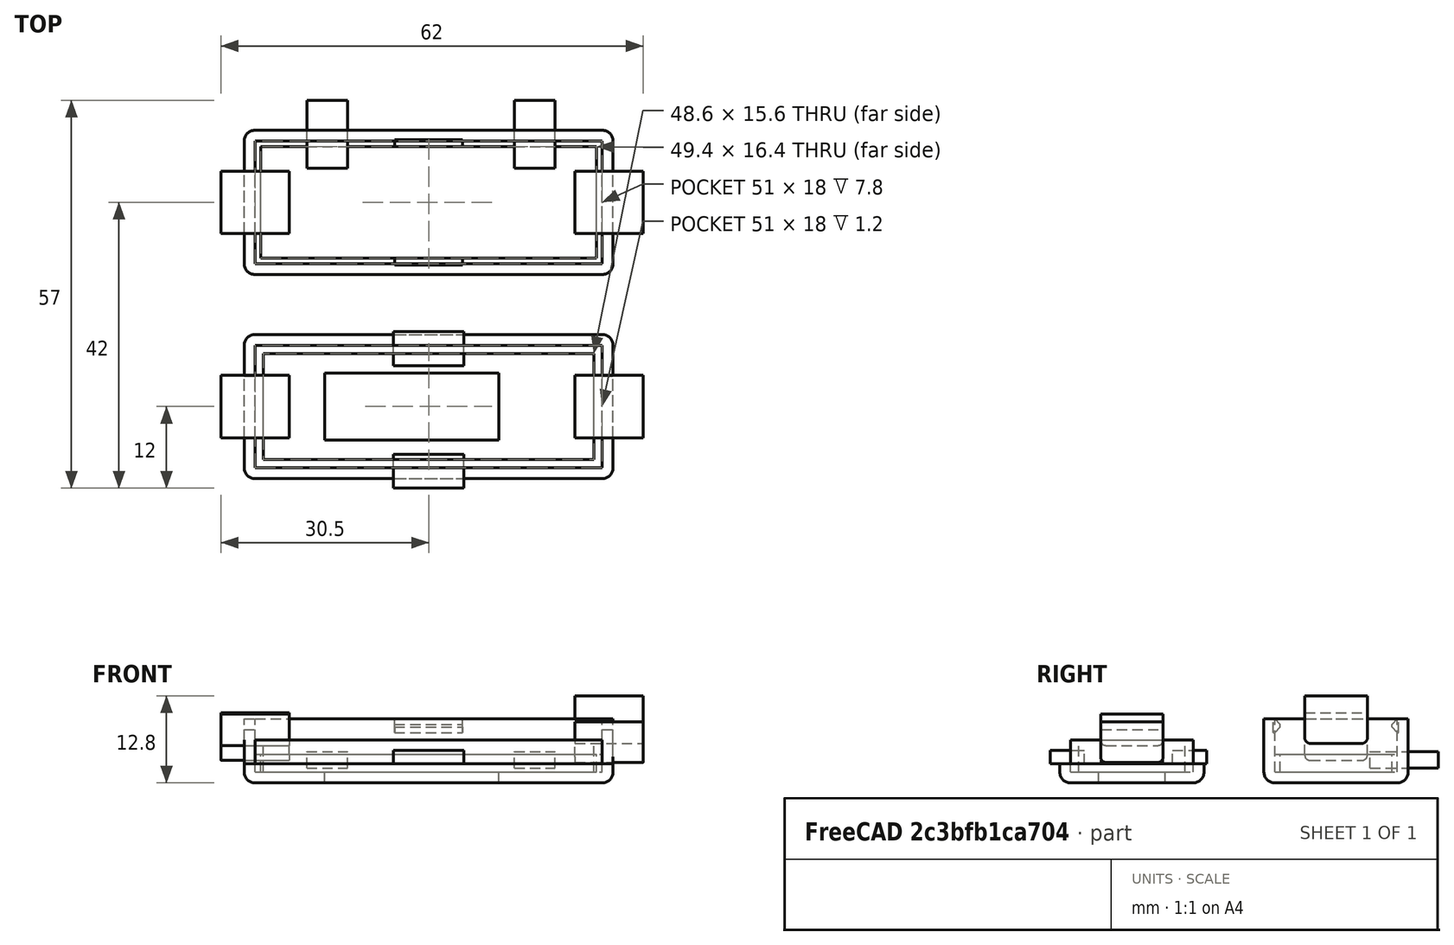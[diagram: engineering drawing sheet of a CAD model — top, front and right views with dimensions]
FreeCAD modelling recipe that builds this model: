
FCSTD DOCUMENT  (FreeCAD 0.16R)
Label: USB-C_Tester_b_raw_v0.4
License: All rights reserved
LicenseURL: http://en.wikipedia.org/wiki/All_rights_reserved
objects: Part::Box×21, Part::Fillet×6, Part::Cut×4, Part::Chamfer×2
note: 33 computed .brp shape members not serialized (recipe doc carries the construction recipe); baked Part::Feature solids carry a one-line shape summary decoded from their .brp

FEATURE [Part::Box] Box  label="unten_außen"
  Height = 9.4
  Length = 54.2
  Placement = pos=(-1.6,-1.6,0) rot=(0,0,1;0rad)
  Width = 21.2
FEATURE [Part::Box] Box001  label="unten_innen"
  Height = 9.4
  Length = 51
  Placement = pos=(0,0,1.6) rot=(0,0,1;0rad)
  Width = 18
FEATURE [Part::Cut] Cut  label="Schale_roh"
  Base = -> Box
  Tool = -> Box001
FEATURE [Part::Fillet] Fillet  label="Schale_unten"
  Base = -> Cut
  Edges = 8 edges r=1.6: [Edge1,Edge3,Edge4,Edge5,Edge6,Edge14,Edge15,Edge16]
FEATURE [Part::Box] Box002  label="Auflage_außen"
  Height = 2.6
  Length = 51
  Placement = pos=(0,0,1.6) rot=(0,0,1;0rad)
  Width = 18
FEATURE [Part::Box] Box003  label="Auflage_innen"
  Height = 2.6
  Length = 49.4
  Placement = pos=(0.8,0.8,1.6) rot=(0,0,1;0rad)
  Width = 16.4
FEATURE [Part::Cut] Cut001  label="Auflage"
  Base = -> Box002
  Tool = -> Box003
FEATURE [Part::Box] Box004  label="Haken1_roh"
  Height = 2
  Length = 10
  Placement = pos=(20.5,-0.2,7.4) rot=(0,0,1;0rad)
  Width = 1
FEATURE [Part::Chamfer] Chamfer  label="Haken1"
  Base = -> Box004
  Edges = 2 edges r=0.8: [Edge11,Edge12]
FEATURE [Part::Box] Box005  label="Haken2_roh"
  Height = 2
  Length = 10
  Placement = pos=(20.5,17.2,7.4) rot=(0,0,1;0rad)
  Width = 1
FEATURE [Part::Chamfer] Chamfer001  label="Haken2"
  Base = -> Box005
  Edges = 2 edges r=0.8: [Edge9,Edge10]
FEATURE [Part::Box] Box006  label="USB_Buchse1_roh"
  Height = 7
  Length = 10
  Placement = pos=(-5,4.4,3.3) rot=(0,0,1;0rad)
  Width = 9.2
FEATURE [Part::Box] Box008  label="Button1"
  Height = 2.4
  Length = 6
  Placement = pos=(7.6,14,2.2) rot=(0,0,1;0rad)
  Width = 10
FEATURE [Part::Box] Box009  label="Button2"
  Height = 2.4
  Length = 6
  Placement = pos=(38.1,14,2.2) rot=(0,0,1;0rad)
  Width = 10
FEATURE [Part::Box] Box010  label="oben_außen"
  Height = 2.8
  Length = 54.2
  Placement = pos=(-1.6,-31.6,0) rot=(0,0,1;0rad)
  Width = 21.2
FEATURE [Part::Box] Box011  label="oben_innen"
  Height = 9.4
  Length = 51
  Placement = pos=(0,-30,1.6) rot=(0,0,1;0rad)
  Width = 18
FEATURE [Part::Cut] Cut002  label="Schale_oben_roh"
  Base = -> Box010
  Tool = -> Box011
FEATURE [Part::Fillet] Fillet001  label="Schale_oben"
  Base = -> Cut002
  Edges = 8 edges r=1.6: [Edge1,Edge3,Edge4,Edge5,Edge6,Edge14,Edge15,Edge16]
FEATURE [Part::Box] Box012  label="Rahmen_außen"
  Height = 4.7
  Length = 51
  Placement = pos=(0,-30,1.6) rot=(0,0,1;0rad)
  Width = 18
FEATURE [Part::Box] Box013  label="Rahmen_innen"
  Height = 4.8
  Length = 48.6
  Placement = pos=(1.2,-28.8,1.6) rot=(0,0,1;0rad)
  Width = 15.6
FEATURE [Part::Cut] Cut003  label="Rahmen"
  Base = -> Box012
  Tool = -> Box013
FEATURE [Part::Box] Box014  label="OLED"
  Height = 1.6
  Length = 25.6
  Placement = pos=(10.2,-25.9,0) rot=(0,0,1;0rad)
  Width = 9.8
FEATURE [Part::Box] Box017  label="Oese1"
  Height = 2
  Length = 10.4
  Placement = pos=(20.3,-33,2.8) rot=(0,0,1;0rad)
  Width = 5
FEATURE [Part::Box] Box018  label="Oese2"
  Height = 2
  Length = 10.4
  Placement = pos=(20.3,-15,2.8) rot=(0,0,1;0rad)
  Width = 5
FEATURE [Part::Box] Box019  label="USB_Buchse2_roh"
  Height = 7
  Length = 10
  Placement = pos=(47,4.4,5.8) rot=(0,0,1;0rad)
  Width = 9.2
FEATURE [Part::Box] Box020  label="USB_Buchse3_roh"
  Height = 4.6
  Length = 10
  Placement = pos=(-5,-25.6,5.5) rot=(0,0,1;0rad)
  Width = 9.2
FEATURE [Part::Box] Box021  label="USB_Buchse4_roh"
  Height = 6
  Length = 10
  Placement = pos=(47,-25.6,3) rot=(0,0,1;0rad)
  Width = 9.2
FEATURE [Part::Fillet] Fillet002  label="USB_Buchse1"
  Base = -> Box006
  Edges = 2 edges r=0.8: [Edge9,Edge11]
FEATURE [Part::Fillet] Fillet003  label="USB_Buchse2"
  Base = -> Box019
  Edges = 2 edges r=0.8: [Edge9,Edge11]
FEATURE [Part::Box] Box022  label="Nut1"
  Height = 5
  Length = 1.6
  Placement = pos=(-1.6,-25.5,2.8) rot=(0,0,1;0rad)
  Width = 9
FEATURE [Part::Box] Box023  label="Nut2"
  Height = 5
  Length = 1.6
  Placement = pos=(51,-25.5,2.8) rot=(0,0,1;0rad)
  Width = 9
FEATURE [Part::Fillet] Fillet004  label="USB-Buchse3"
  Base = -> Box020
  Edges = 2 edges r=0.8: [Edge9,Edge11]
FEATURE [Part::Fillet] Fillet005  label="USB-Buchse4"
  Base = -> Box021
  Edges = 2 edges r=0.8: [Edge9,Edge11]
